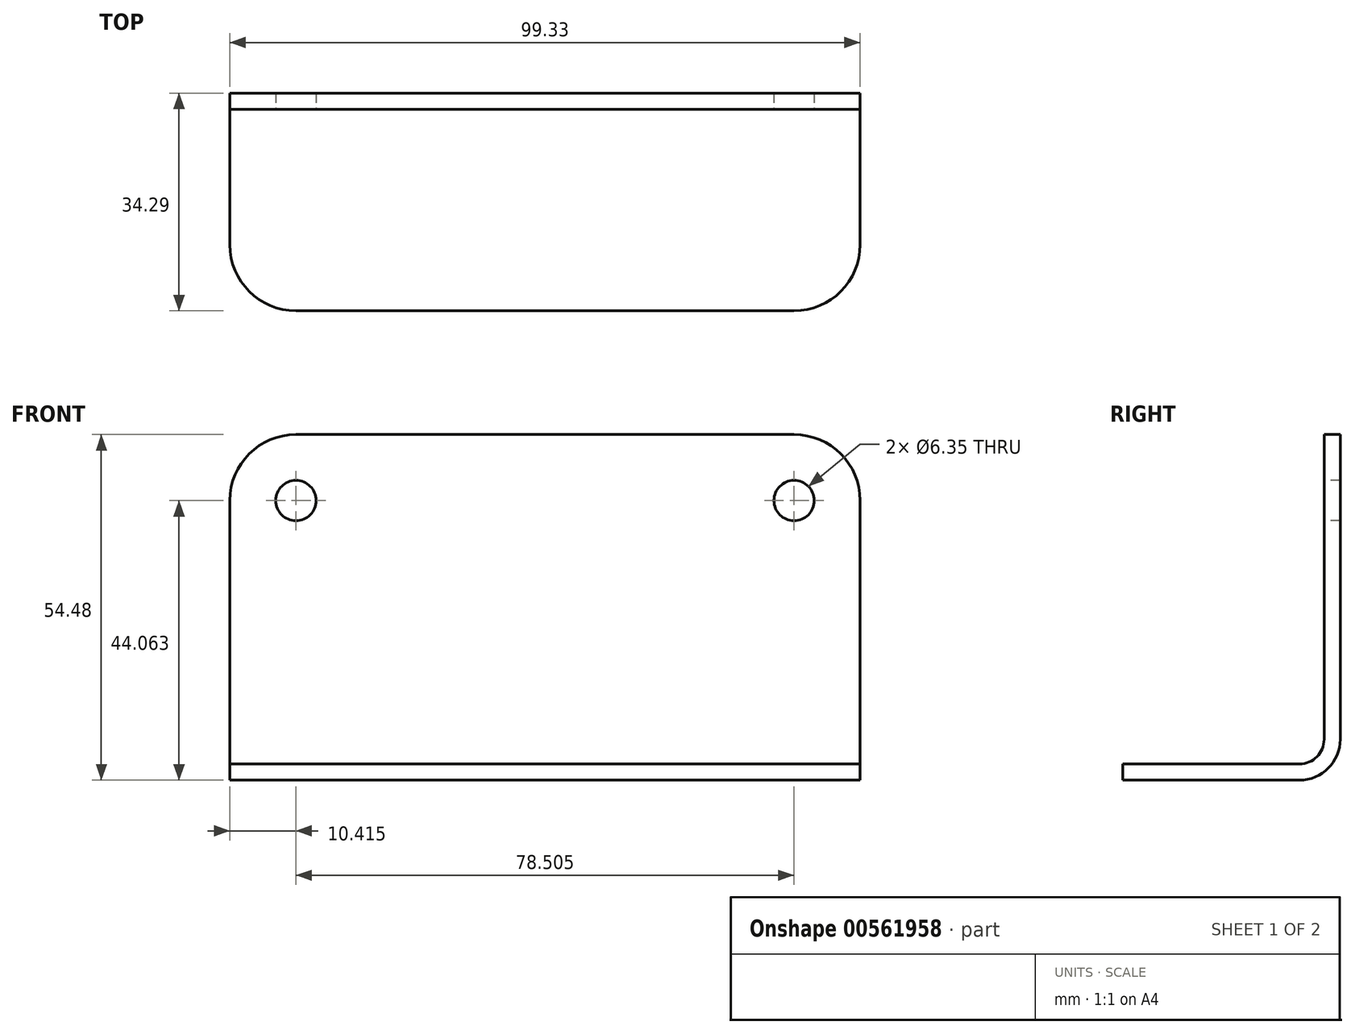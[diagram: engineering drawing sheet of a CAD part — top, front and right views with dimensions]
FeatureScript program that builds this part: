
annotation { "Feature Type Name" : "Feature", "Feature Type Description" : "" }
export const myFeature = defineFeature(function(context is Context, id is Id, definition is map)
    precondition{}
    {
        {
            var Q0;
            Q0=qCreatedBy(makeId("Front.planeOp"),FACE);
            var sketch = newSketch(context, id + "F0", { "sketchPlane" : qUnion([Q0])});
            skLineSegment(sketch, "E0.bottom", {"start": v(-27.42, 28.2) * mm, "end": v(71.91, 28.2) * mm});
            skLineSegment(sketch, "E0.top", {"start": v(-27.42, -26.28) * mm, "end": v(71.91, -26.28) * mm});
            skLineSegment(sketch, "E0.left", {"start": v(-27.42, 28.2) * mm, "end": v(-27.42, -26.28) * mm});
            skLineSegment(sketch, "E0.right", {"start": v(71.91, 28.2) * mm, "end": v(71.91, -26.28) * mm});
            skSolve(sketch);
        }
        {
            var Q0;
            Q0=makeQuery(id+"F0.imprint","IMPRINT",FACE,{"disambiguationData":[TD([[makeQuery(id+"F0.imprint","IMPRINT",EDGE,{"derivedFrom":sQuery(id+"F0.wireOp",EDGE,"E0.bottom")}),-1.0]])]});
            extrude(context, id + "F1", {"entities" : qUnion([Q0]), "depth" : 34.3 * mm, "offsetDistance" : 25.4 * mm});
        }
        {
            var Q0;
            Q0=makeQuery(id+"F1.opExtrude","SWEPT_EDGE",EDGE,{"disambiguationData":[OSD([sQuery(id+"F0.wireOp",EDGE,"E0.bottom"),sQuery(id+"F0.wireOp",EDGE,"E0.right")])]});
            var Q1;
            Q1=makeQuery(id+"F1.opExtrude","SWEPT_EDGE",EDGE,{"disambiguationData":[OSD([sQuery(id+"F0.wireOp",EDGE,"E0.bottom"),sQuery(id+"F0.wireOp",EDGE,"E0.left")])]});
            var Q2;
            Q2=makeQuery(id+"F1.opExtrude","CAP_EDGE",EDGE,{"disambiguationData":[OSD([sQuery(id+"F0.wireOp",EDGE,"E0.right")])],"isStart":false});
            var Q3;
            Q3=makeQuery(id+"F1.opExtrude","CAP_EDGE",EDGE,{"disambiguationData":[OSD([sQuery(id+"F0.wireOp",EDGE,"E0.left")])],"isStart":false});
            fillet(context, id + "F2", {"entities" : qUnion([Q0, Q1, Q2, Q3]), "radius" : 10.4 * mm, "tangentPropagation" : true, "allowEdgeOverflow" : false});
        }
        {
            var Q0;
            Q0=makeQuery(id+"F1.opExtrude","CAP_EDGE",EDGE,{"disambiguationData":[OSD([sQuery(id+"F0.wireOp",EDGE,"E0.top")])],"isStart":true});
            fillet(context, id + "F3", {"entities" : qUnion([Q0]), "radius" : 6.43 * mm, "tangentPropagation" : true, "allowEdgeOverflow" : false});
        }
        {
            var Q0;
            Q0=makeQuery(id+"F1.opExtrude","CAP_FACE",FACE,{"disambiguationData":[OSD([sQuery(id+"F0.wireOp",EDGE,"E0.bottom"),sQuery(id+"F0.wireOp",EDGE,"E0.top"),sQuery(id+"F0.wireOp",EDGE,"E0.left"),sQuery(id+"F0.wireOp",EDGE,"E0.right")])],"isStart":false});
            var Q1;
            Q1=makeQuery(id+"F1.opExtrude","SWEPT_FACE",FACE,{"disambiguationData":[OSD([sQuery(id+"F0.wireOp",EDGE,"E0.bottom")])]});
            var Q2;
            Q2=makeQuery(id+"F2.opFillet","BLEND_FACE",FACE,{"disambiguationData":[OSD([sQuery(id+"F0.wireOp",EDGE,"E0.bottom"),sQuery(id+"F0.wireOp",EDGE,"E0.right")])]});
            var Q3;
            Q3=makeQuery(id+"F2.opFillet","BLEND_FACE",FACE,{"disambiguationData":[OSD([sQuery(id+"F0.wireOp",EDGE,"E0.right")])]});
            var Q4;
            Q4=makeQuery(id+"F1.opExtrude","SWEPT_FACE",FACE,{"disambiguationData":[OSD([sQuery(id+"F0.wireOp",EDGE,"E0.right")])]});
            var Q5;
            Q5=makeQuery(id+"F2.opFillet","BLEND_FACE",FACE,{"disambiguationData":[OSD([sQuery(id+"F0.wireOp",EDGE,"E0.left")])]});
            var Q6;
            Q6=makeQuery(id+"F2.opFillet","BLEND_FACE",FACE,{"disambiguationData":[OSD([sQuery(id+"F0.wireOp",EDGE,"E0.bottom"),sQuery(id+"F0.wireOp",EDGE,"E0.left")])]});
            var Q7;
            Q7=makeQuery(id+"F1.opExtrude","SWEPT_FACE",FACE,{"disambiguationData":[OSD([sQuery(id+"F0.wireOp",EDGE,"E0.left")])]});
            shell(context, id + "F4", {"entities" : qUnion([Q0, Q1, Q2, Q3, Q4, Q5, Q6, Q7]), "thickness" : 2.54 * mm});
        }
        {
            var Q0;
            Q0=makeQuery(id+"F4.opShell","OFFSET_FACE",FACE,{"disambiguationData":[OSD([sQuery(id+"F0.wireOp",EDGE,"E0.bottom"),sQuery(id+"F0.wireOp",EDGE,"E0.top"),sQuery(id+"F0.wireOp",EDGE,"E0.left"),sQuery(id+"F0.wireOp",EDGE,"E0.right")])]});
            var sketch = newSketch(context, id + "F5", { "sketchPlane" : qUnion([Q0])});
            skPoint(sketch, "E1", {"position": v(-17, 17.78) * mm});
            skPoint(sketch, "E2", {"position": v(61.5, 17.78) * mm});
            skSolve(sketch);
        }
        {
            var Q0;
            Q0=sQuery(id+"F5.wireOp",VERTEX,"E1");
            var Q1;
            Q1=sQuery(id+"F5.wireOp",VERTEX,"E2");
            var Q2;
            Q2=makeQuery(id+"F1.opExtrude","SWEPT_BODY",BODY,{"disambiguationData":[OSD([sQuery(id+"F0.wireOp",EDGE,"E0.bottom"),sQuery(id+"F0.wireOp",EDGE,"E0.top"),sQuery(id+"F0.wireOp",EDGE,"E0.left"),sQuery(id+"F0.wireOp",EDGE,"E0.right")])]});
            hole(context, id + "F6", {"style" : HoleStyle.SIMPLE, "endStyle" : HoleEndStyle.THROUGH, "holeDiameter" : 6.35 * mm, "majorDiameter" : 6.35 * mm, "isTappedThrough" : true, "tappedDepth" : 12.7 * mm, "tapClearance" : 3, "locations" : qUnion([Q0, Q1]), "scope" : qUnion([Q2])});
        }
    });
